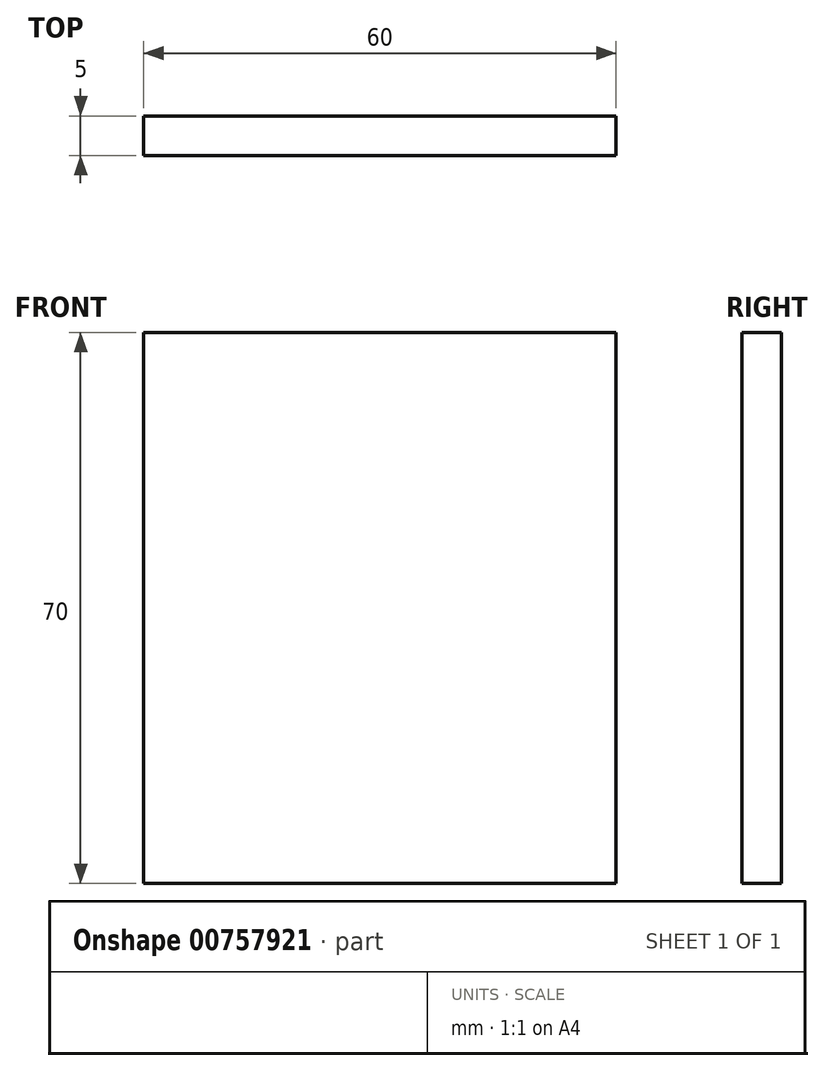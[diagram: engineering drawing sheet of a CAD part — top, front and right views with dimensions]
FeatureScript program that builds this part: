
annotation { "Feature Type Name" : "Feature", "Feature Type Description" : "" }
export const myFeature = defineFeature(function(context is Context, id is Id, definition is map)
    precondition{}
    {
        {
            var Q0;
            Q0=qCreatedBy(makeId("Front.planeOp"),FACE);
            var sketch = newSketch(context, id + "F0", { "sketchPlane" : qUnion([Q0])});
            skLineSegment(sketch, "E0.top", {"start": v(-48.3, -23.3) * mm, "end": v(11.7, -23.3) * mm});
            skLineSegment(sketch, "E0.left", {"start": v(-48.3, 46.7) * mm, "end": v(-48.3, -23.3) * mm});
            skLineSegment(sketch, "E1.bottom", {"start": v(-48.3, 46.7) * mm, "end": v(11.7, 46.7) * mm});
            skLineSegment(sketch, "E1.right", {"start": v(11.7, 46.7) * mm, "end": v(11.7, -23.3) * mm});
            skSolve(sketch);
        }
        {
            var Q0;
            Q0 = qSketchRegion(id + "F0", true);
            extrude(context, id + "F1", {"entities" : qUnion([Q0]), "depth" : 5 * mm, "offsetDistance" : 25 * mm});
        }
    });
